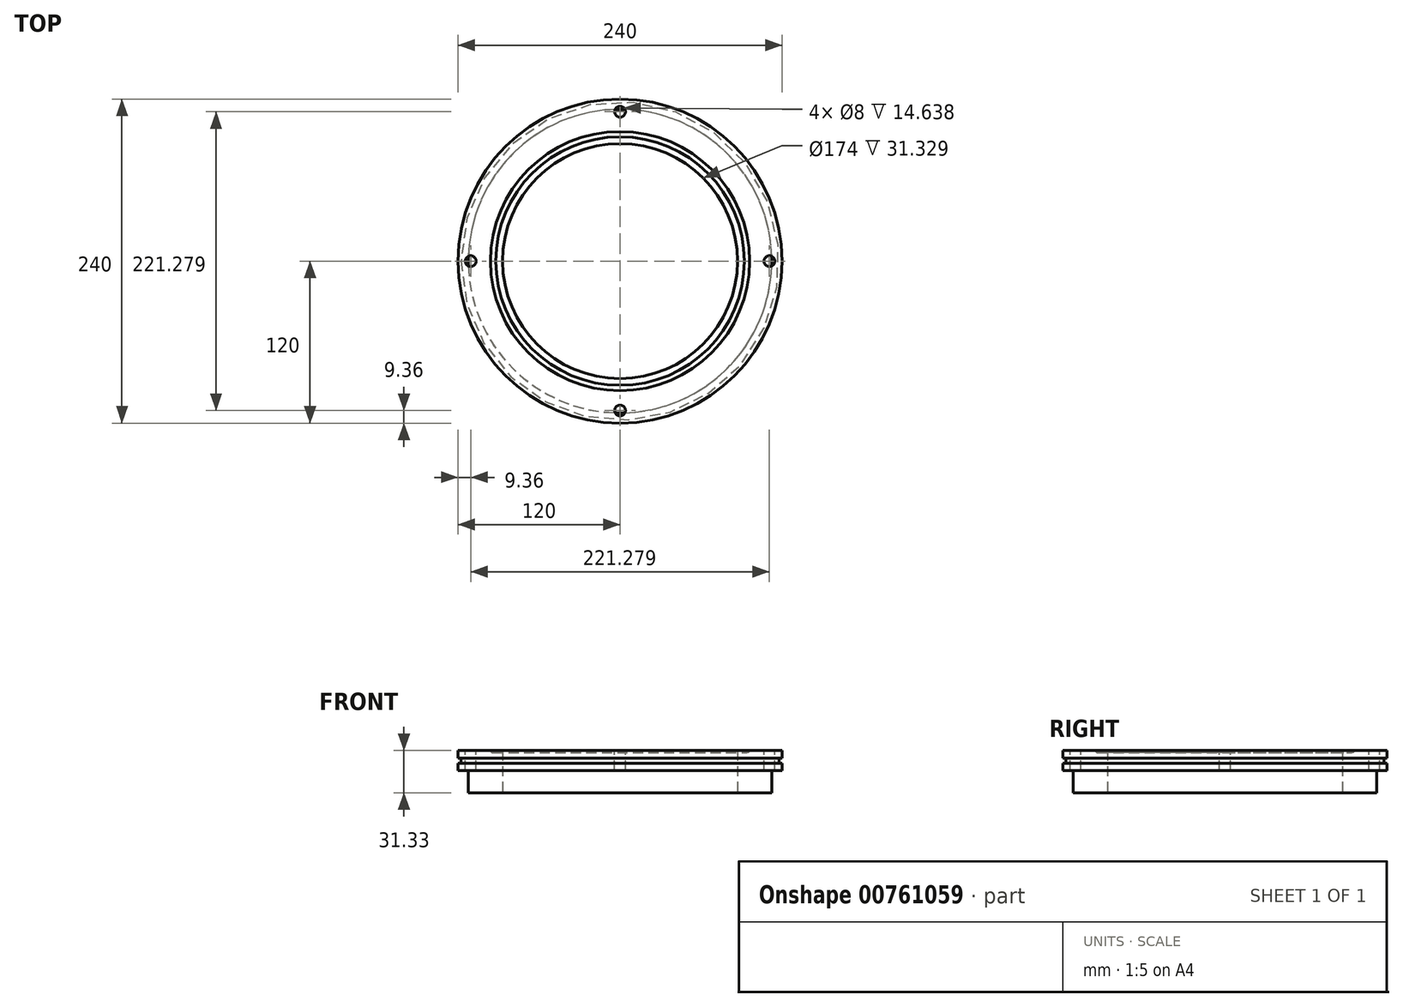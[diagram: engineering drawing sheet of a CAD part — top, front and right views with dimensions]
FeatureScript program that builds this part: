
annotation { "Feature Type Name" : "Feature", "Feature Type Description" : "" }
export const myFeature = defineFeature(function(context is Context, id is Id, definition is map)
    precondition{}
    {
        {
            var Q0;
            Q0=qCreatedBy(makeId("Front.planeOp"),FACE);
            var sketch = newSketch(context, id + "F0", { "sketchPlane" : qUnion([Q0])});
            skLineSegment(sketch, "E0", {"start": v(112.41, 0) * mm, "end": v(112.41, 16.7) * mm});
            skLineSegment(sketch, "E1", {"start": v(112.41, 16.7) * mm, "end": v(120, 16.7) * mm});
            skLineSegment(sketch, "E2", {"start": v(92, 31.33) * mm, "end": v(87, 31.33) * mm});
            skLineSegment(sketch, "E3", {"start": v(87, 31.33) * mm, "end": v(87, 0) * mm});
            skLineSegment(sketch, "E4", {"start": v(87, 0) * mm, "end": v(112.41, 0) * mm});
            skLineSegment(sketch, "E5", {"start": v(0, -74.95) * mm, "end": v(0, 76.27) * mm});
            skLineSegment(sketch, "E6", {"start": v(95.92, 31.33) * mm, "end": v(120, 31.33) * mm});
            skArc(sketch, "E7", {"start": v(92, 31.33) * mm, "mid": v(93.96, 29.72) * mm, "end": v(95.92, 31.33) * mm});
            skLineSegment(sketch, "E8", {"start": v(120, 31.33) * mm, "end": v(120, 25.83) * mm});
            skLineSegment(sketch, "E9", {"start": v(120, 16.7) * mm, "end": v(120, 21.86) * mm});
            skArc(sketch, "E10", {"start": v(120, 25.83) * mm, "mid": v(117.76, 23.85) * mm, "end": v(120, 21.86) * mm});
            skSolve(sketch);
        }
        {
            var Q0;
            Q0=makeQuery(id+"F0.imprint","IMPRINT",FACE,{"disambiguationData":[TD([[makeQuery(id+"F0.imprint","IMPRINT",EDGE,{"derivedFrom":sQuery(id+"F0.wireOp",EDGE,"E0")}),1.0]])]});
            var Q1;
            Q1=sQuery(id+"F0.wireOp",EDGE,"E5");
            revolve(context, id + "F1", {"surfaceOperationType" : NewSurfaceOperationType.NEW, "entities" : qUnion([Q0]), "axis" : qUnion([Q1]), "revolveType" : RevolveType.FULL});
        }
        {
            var Q0;
            Q0=makeQuery(id+"F1.opRevolve","SWEPT_FACE",FACE,{"disambiguationData":[OSD([sQuery(id+"F0.wireOp",EDGE,"E6")])]});
            var sketch = newSketch(context, id + "F2", { "sketchPlane" : qUnion([Q0])});
            skCircle(sketch, "E11", {"center": v(110.64, 0) * mm, "radius": 4 * mm});
            skCircle(sketch, "E12", {"center": v(-110.64, 0) * mm, "radius": 4 * mm});
            skCircle(sketch, "E13", {"center": v(0, 110.64) * mm, "radius": 4 * mm});
            skCircle(sketch, "E14", {"center": v(0, -110.64) * mm, "radius": 4 * mm});
            skSolve(sketch);
        }
        {
            var Q0;
            Q0 = qSketchRegion(id + "F2", true);
            var Q1;
            Q1=makeQuery(id+"F1.opRevolve","SWEPT_FACE",FACE,{"disambiguationData":[OSD([sQuery(id+"F0.wireOp",EDGE,"E1")])]});
            extrude(context, id + "F3", {"entities" : qUnion([Q0]), "operationType" : NewBodyOperationType.REMOVE, "endBound" : BoundingType.UP_TO_SURFACE, "oppositeDirection" : true, "depth" : 25 * mm, "endBoundEntityFace" : qUnion([Q1]), "offsetDistance" : 25 * mm});
        }
    });
